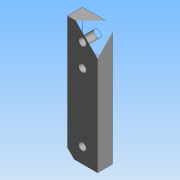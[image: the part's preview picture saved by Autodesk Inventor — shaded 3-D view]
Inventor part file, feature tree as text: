
AUTODESK INVENTOR PART (.ipt)
format: ipt  version: 2015 (Build 190159000, 159)  size: 94,208 bytes
history: native  units: mm
features: extrude x2, projected_geometry x1
ambient origin geometry x8: Origin, YZ Plane, XZ Plane, XY Plane, X Axis, Y Axis, Z Axis, Center Point
bodies: Solid1 (feature_tree)
feature tree (3):
  extrude  "Extrusion1"  Depth=80.0mm
  extrude  "Extrusion3"  Depth=10.0mm TaperAngle=0.0deg
  projected_geometry  "Projected Loop1"
